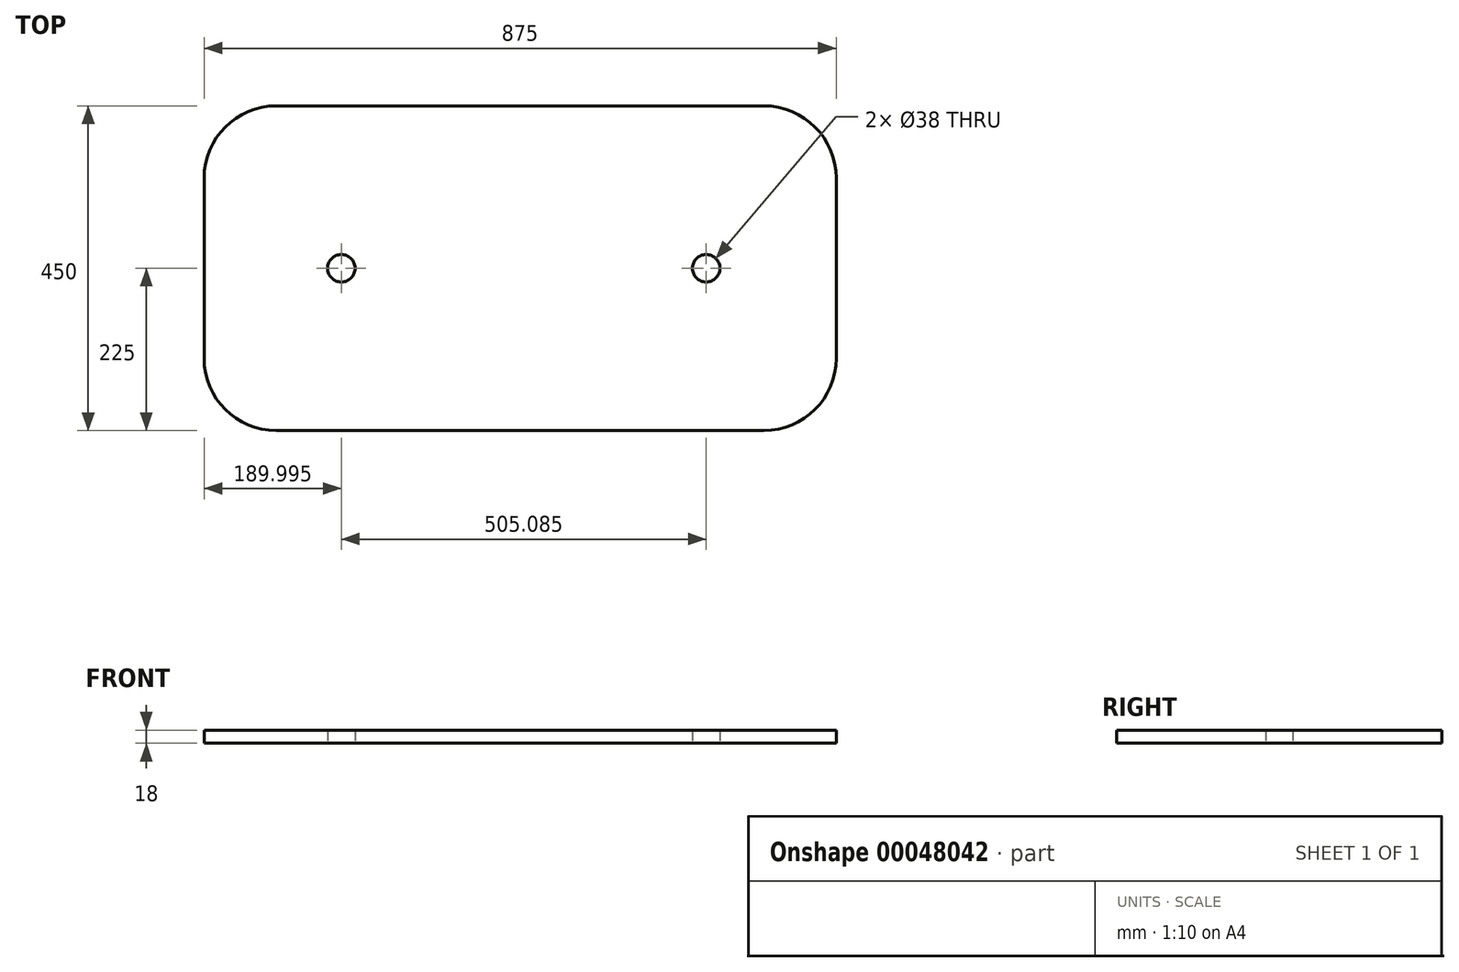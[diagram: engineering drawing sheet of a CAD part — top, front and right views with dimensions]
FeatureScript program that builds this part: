
annotation { "Feature Type Name" : "Feature", "Feature Type Description" : "" }
export const myFeature = defineFeature(function(context is Context, id is Id, definition is map)
    precondition{}
    {
        {
            var Q0;
            Q0=qCreatedBy(makeId("Top.planeOp"),FACE);
            var sketch = newSketch(context, id + "F0", { "sketchPlane" : qUnion([Q0])});
            skLineSegment(sketch, "E0.0", {"start": v(-595.08, 225) * mm, "end": v(79.92, 225) * mm});
            skLineSegment(sketch, "E0.4", {"start": v(-595.08, -225) * mm, "end": v(79.92, -225) * mm});
            skCircle(sketch, "E1", {"center": v(-505.08, 0) * mm, "radius": 19 * mm});
            skCircle(sketch, "E2", {"center": v(0, 0) * mm, "radius": 19 * mm});
            skLineSegment(sketch, "E3", {"start": v(179.92, -125) * mm, "end": v(179.92, 125) * mm});
            skPoint(sketch, "E4.visualSharp", {"position": v(179.92, 225) * mm});
            skArc(sketch, "E4.filletArc", {"start": v(179.92, 125) * mm, "mid": v(150.63, 195.71) * mm, "end": v(79.92, 225) * mm});
            skPoint(sketch, "E5.visualSharp", {"position": v(-710.1, -225) * mm});
            skLineSegment(sketch, "E6", {"start": v(-695.08, -125) * mm, "end": v(-695.08, 125) * mm});
            skPoint(sketch, "E7.visualSharp", {"position": v(-695.08, 225) * mm});
            skArc(sketch, "E7.filletArc", {"start": v(-595.08, 225) * mm, "mid": v(-665.8, 195.71) * mm, "end": v(-695.08, 125) * mm});
            skPoint(sketch, "E8.visualSharp", {"position": v(-695.08, -225) * mm});
            skArc(sketch, "E8.filletArc", {"start": v(-695.08, -125) * mm, "mid": v(-665.8, -195.71) * mm, "end": v(-595.08, -225) * mm});
            skPoint(sketch, "E9.visualSharp", {"position": v(179.92, -225) * mm});
            skArc(sketch, "E9.filletArc", {"start": v(79.92, -225) * mm, "mid": v(150.63, -195.71) * mm, "end": v(179.92, -125) * mm});
            skSolve(sketch);
        }
        {
            var Q0;
            Q0 = qSketchRegion(id + "F0", true);
            extrude(context, id + "F1", {"entities" : qUnion([Q0]), "depth" : 18 * mm});
        }
    });
